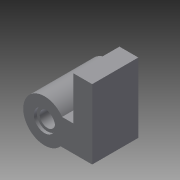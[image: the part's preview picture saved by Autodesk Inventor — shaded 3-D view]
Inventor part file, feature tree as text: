
AUTODESK INVENTOR PART (.ipt)
format: ipt  version: 2015 (Build 190159000, 159)  size: 120,832 bytes
history: native  units: in
note: dims shown in document units (in); Inventor stores cm internally (conversion verified against a paired STEP export)
features: extrude x4, sketch x4, reference x1
ambient origin geometry x8: Origin, YZ Plane, XZ Plane, XY Plane, X Axis, Y Axis, Z Axis, Center Point
bodies: Solid1 (feature_tree)
feature tree (9):
  extrude  "Extrusion1"  Depth=0.9375in TaperAngle=0.0deg
  extrude  "Extrusion2"  Depth=0.4882in TaperAngle=0.0deg
  extrude  "Extrusion3"  Depth=0.0591in TaperAngle=0.0deg
  extrude  "Extrusion4"  [1 undecoded]
  sketch  "Sketch1"  dims[d0=0.375in d1=0.0in d2=0.9375in d3=0.0in]
  reference  "Reference1"
  sketch  "Sketch2"  dims[d4=0.3125in d5=0.4882in d6=0.0in]
  sketch  "Sketch3"  dims[d7=0.4331in d8=0.0591in d9=0.0in]
  sketch  "Sketch4"
note: 1 required parameter value undecoded (feature->parameter linkage not recoverable at this tier; creation-order binding heuristic only, values carry confidence <= 0.55)
